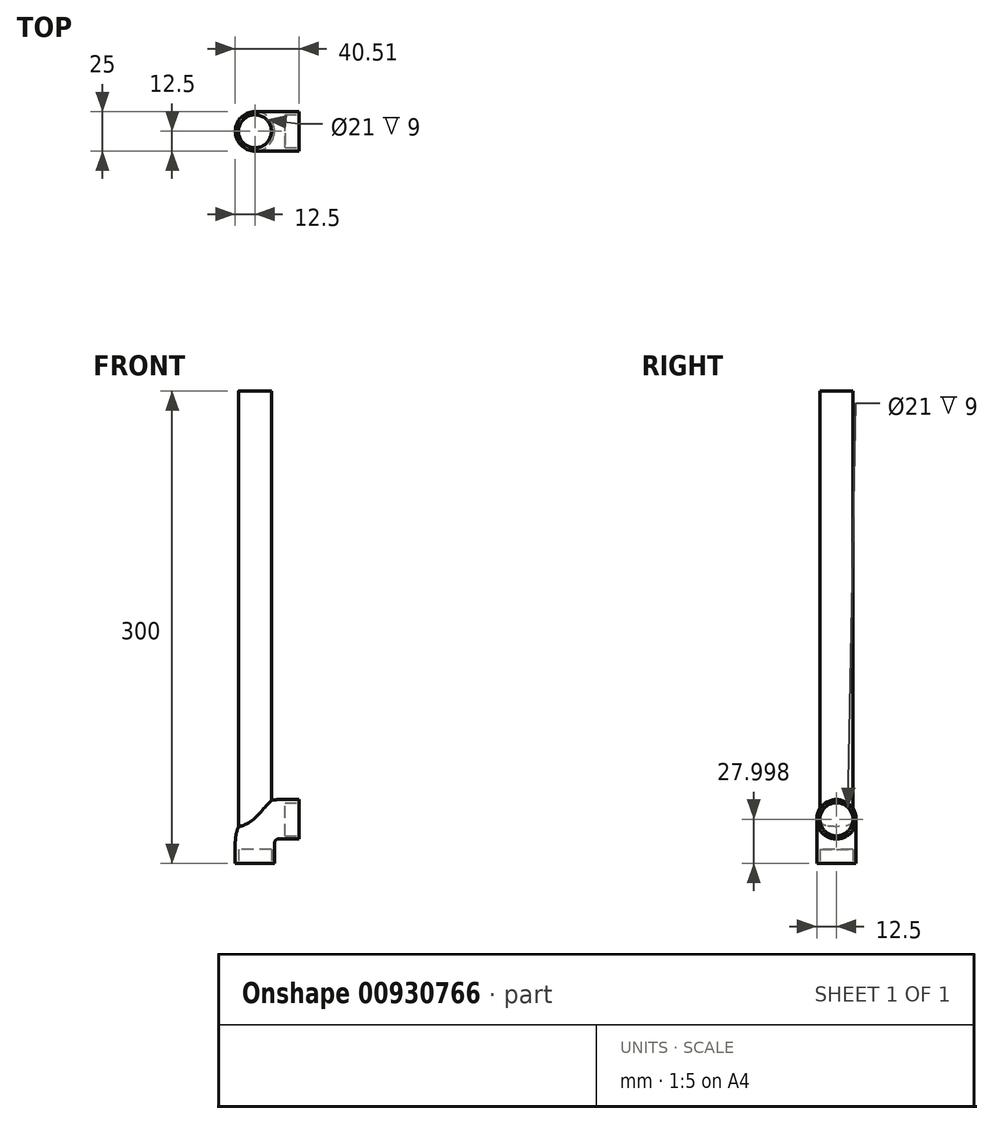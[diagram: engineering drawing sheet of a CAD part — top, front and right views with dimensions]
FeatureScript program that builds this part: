
annotation { "Feature Type Name" : "Feature", "Feature Type Description" : "" }
export const myFeature = defineFeature(function(context is Context, id is Id, definition is map)
    precondition{}
    {
        {
            var Q0;
            Q0=qCreatedBy(makeId("Top.planeOp"),FACE);
            var sketch = newSketch(context, id + "F0", { "sketchPlane" : qUnion([Q0])});
            skCircle(sketch, "E0", {"center": v(0, 0) * mm, "radius": 10.5 * mm});
            skSolve(sketch);
        }
        {
            var Q0;
            Q0=qCreatedBy(makeId("Top.planeOp"),FACE);
            var sketch = newSketch(context, id + "F1", { "sketchPlane" : qUnion([Q0])});
            skCircle(sketch, "E1", {"center": v(0, 0) * mm, "radius": 12.5 * mm});
            skSolve(sketch);
        }
        {
            var Q0;
            Q0 = qSketchRegion(id + "F0", true);
            extrude(context, id + "F2", {"entities" : qUnion([Q0]), "depth" : 40 * mm, "offsetDistance" : 25 * mm});
        }
        {
            var Q0;
            Q0 = qSketchRegion(id + "F0", true);
            extrude(context, id + "F3", {"entities" : qUnion([Q0]), "depth" : 50 * mm, "offsetDistance" : 25 * mm});
        }
        {
            var Q0;
            Q0 = qSketchRegion(id + "F0", true);
            extrude(context, id + "F4", {"entities" : qUnion([Q0]), "depth" : 60 * mm, "offsetDistance" : 25 * mm});
        }
        {
            var Q0;
            Q0 = qSketchRegion(id + "F0", true);
            extrude(context, id + "F5", {"entities" : qUnion([Q0]), "depth" : 80 * mm, "offsetDistance" : 25 * mm});
        }
        {
            var Q0;
            Q0 = qSketchRegion(id + "F0", true);
            extrude(context, id + "F6", {"entities" : qUnion([Q0]), "depth" : 100 * mm, "offsetDistance" : 25 * mm});
        }
        {
            var Q0;
            Q0 = qSketchRegion(id + "F0", true);
            extrude(context, id + "F7", {"entities" : qUnion([Q0]), "depth" : 120 * mm, "offsetDistance" : 25 * mm});
        }
        {
            var Q0;
            Q0 = qSketchRegion(id + "F0", true);
            extrude(context, id + "F8", {"entities" : qUnion([Q0]), "depth" : 150 * mm, "offsetDistance" : 25 * mm});
        }
        {
            var Q0;
            Q0 = qSketchRegion(id + "F0", true);
            extrude(context, id + "F9", {"entities" : qUnion([Q0]), "depth" : 180 * mm, "offsetDistance" : 25 * mm});
        }
        {
            var Q0;
            Q0 = qSketchRegion(id + "F0", true);
            extrude(context, id + "F10", {"entities" : qUnion([Q0]), "depth" : 200 * mm, "offsetDistance" : 25 * mm});
        }
        {
            var Q0;
            Q0 = qSketchRegion(id + "F0", true);
            extrude(context, id + "F11", {"entities" : qUnion([Q0]), "depth" : 300 * mm, "offsetDistance" : 25 * mm});
        }
        {
            var Q0;
            Q0=qCreatedBy(makeId("Front.planeOp"),FACE);
            var sketch = newSketch(context, id + "F12", { "sketchPlane" : qUnion([Q0])});
            skLineSegment(sketch, "E2", {"start": v(0, 0) * mm, "end": v(0, 13) * mm});
            skLineSegment(sketch, "E3", {"start": v(15, 28) * mm, "end": v(28, 28) * mm, "construction": true});
            skPoint(sketch, "E4.visualSharp", {"position": v(0, 28) * mm});
            skArc(sketch, "E4.filletArc", {"start": v(15, 28) * mm, "mid": v(9.26, 26.86) * mm, "end": v(4.4, 23.6) * mm, "construction": true});
            skPoint(sketch, "E5", {"position": v(4.4, 23.6) * mm});
            skArc(sketch, "E6", {"start": v(4.4, 23.6) * mm, "mid": v(1.14, 18.74) * mm, "end": v(0, 13) * mm});
            skSolve(sketch);
        }
        {
            var Q0;
            Q0 = qSketchRegion(id + "F1", true);
            var Q1;
            Q1 = qConstructionFilter(qBodyType(qCreatedBy(id + "F12" ,EDGE), BodyType.WIRE), ConstructionObject.NO);
            sweep(context, id + "F13", {"profiles" : qUnion([Q0]), "path" : qUnion([Q1])});
        }
        {
            var Q0;
            Q0 = qSketchRegion(id + "F0", true);
            extrude(context, id + "F14", {"entities" : qUnion([Q0]), "operationType" : NewBodyOperationType.REMOVE, "depth" : 9 * mm, "offsetDistance" : 25 * mm});
        }
        {
            var Q0;
            Q0=makeQuery(id+"F13.opSweep","SWEPT_BODY",BODY,{"disambiguationData":[OSD([sQuery(id+"F1.wireOp",EDGE,"E1"),sQuery(id+"F12.wireOp",EDGE,"E6")])]});
            var Q1;
            Q1=makeQuery(id+"F13.opSweep","CAP_FACE",FACE,{"disambiguationData":[OSD([sQuery(id+"F1.wireOp",EDGE,"E1"),sQuery(id+"F12.wireOp",VERTEX,"E6.start")])],"isStart":false});
            mirror(context, id + "F15", {"operationType" : NewBodyOperationType.ADD, "entities" : qUnion([Q0]), "mirrorPlane" : qUnion([Q1])});
        }
    });
